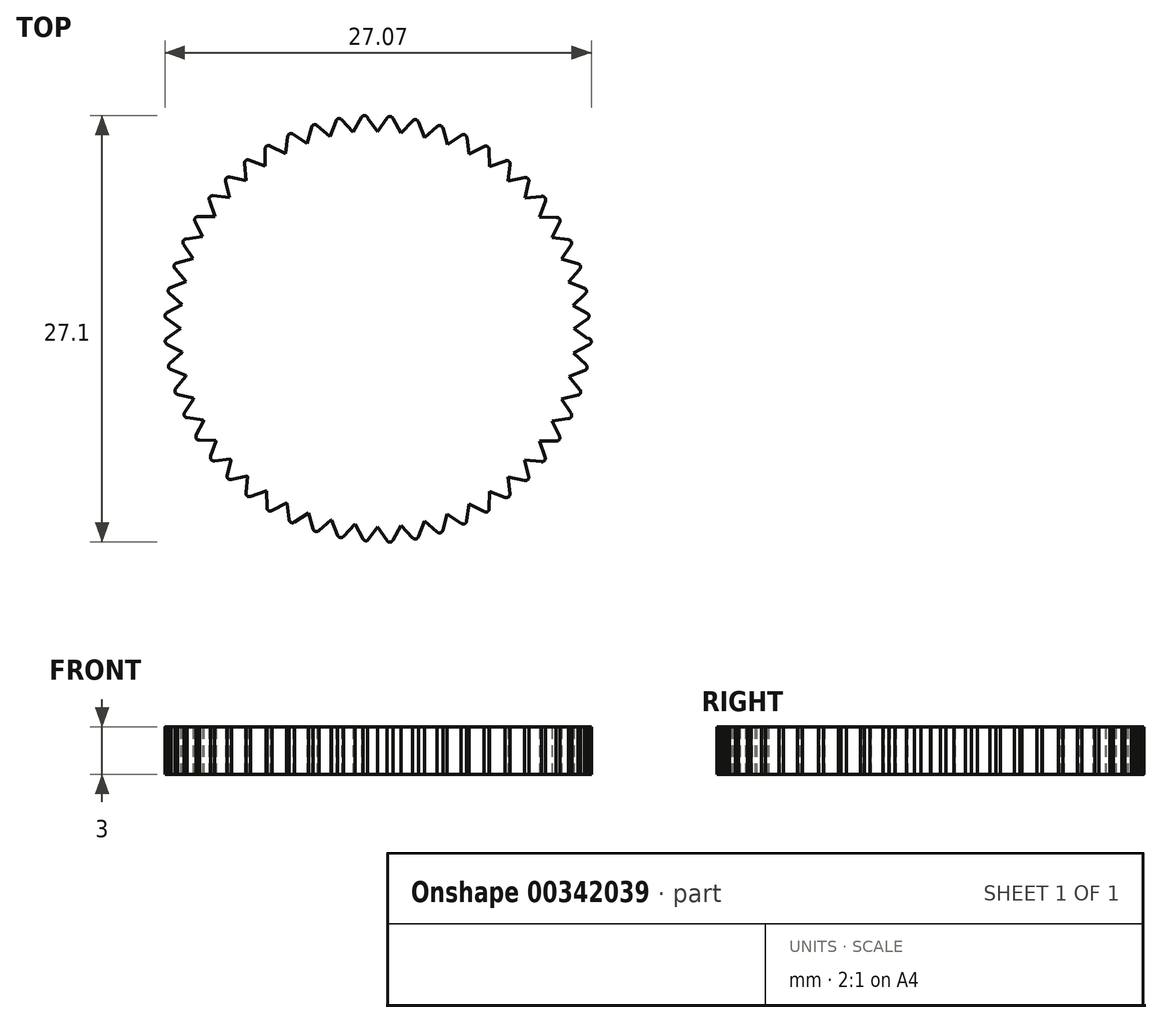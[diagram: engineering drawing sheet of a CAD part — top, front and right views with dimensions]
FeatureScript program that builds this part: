
annotation { "Feature Type Name" : "Feature", "Feature Type Description" : "" }
export const myFeature = defineFeature(function(context is Context, id is Id, definition is map)
    precondition{}
    {
        {
            var Q0;
            Q0=qCreatedBy(makeId("Top.planeOp"),FACE);
            var sketch = newSketch(context, id + "F0", { "sketchPlane" : qUnion([Q0])});
            skCircle(sketch, "E0", {"center": v(0, 0) * mm, "radius": 12.5 * mm});
            skPoint(sketch, "E1", {"position": v(1.51, 12.4) * mm});
            skPoint(sketch, "E2", {"position": v(0, 12.5) * mm});
            skArc(sketch, "E3", {"start": v(1, 13.35) * mm, "mid": v(0.82, 13.47) * mm, "end": v(0.62, 13.37) * mm});
            skLineSegment(sketch, "E4", {"start": v(0.62, 13.37) * mm, "end": v(0, 12.5) * mm});
            skLineSegment(sketch, "E5", {"start": v(1, 13.35) * mm, "end": v(1.51, 12.4) * mm});
            skPoint(sketch, "E6", {"position": v(3, 12.12) * mm});
            skArc(sketch, "E7", {"start": v(2.61, 13.12) * mm, "mid": v(2.45, 13.27) * mm, "end": v(2.24, 13.2) * mm});
            skLineSegment(sketch, "E8", {"start": v(2.24, 13.2) * mm, "end": v(1.51, 12.4) * mm});
            skLineSegment(sketch, "E9", {"start": v(2.61, 13.12) * mm, "end": v(3, 12.12) * mm});
            skPoint(sketch, "E10", {"position": v(4.45, 11.7) * mm});
            skArc(sketch, "E11", {"start": v(4.16, 12.72) * mm, "mid": v(4.01, 12.89) * mm, "end": v(3.8, 12.83) * mm});
            skLineSegment(sketch, "E12", {"start": v(3.8, 12.83) * mm, "end": v(3, 12.12) * mm});
            skLineSegment(sketch, "E13", {"start": v(4.16, 12.72) * mm, "end": v(4.45, 11.7) * mm});
            skPoint(sketch, "E14", {"position": v(5.82, 11.07) * mm});
            skArc(sketch, "E15", {"start": v(5.68, 12.13) * mm, "mid": v(5.56, 12.31) * mm, "end": v(5.34, 12.28) * mm});
            skLineSegment(sketch, "E16", {"start": v(5.34, 12.28) * mm, "end": v(4.45, 11.7) * mm});
            skLineSegment(sketch, "E17", {"start": v(5.68, 12.13) * mm, "end": v(5.82, 11.07) * mm});
            skPoint(sketch, "E18", {"position": v(7.12, 10.3) * mm});
            skArc(sketch, "E19", {"start": v(7.1, 11.36) * mm, "mid": v(7, 11.56) * mm, "end": v(6.78, 11.55) * mm});
            skLineSegment(sketch, "E20", {"start": v(6.78, 11.55) * mm, "end": v(5.82, 11.07) * mm});
            skLineSegment(sketch, "E21", {"start": v(7.1, 11.36) * mm, "end": v(7.12, 10.3) * mm});
            skPoint(sketch, "E22", {"position": v(8.3, 9.35) * mm});
            skArc(sketch, "E23", {"start": v(8.43, 10.41) * mm, "mid": v(8.35, 10.62) * mm, "end": v(8.13, 10.65) * mm});
            skLineSegment(sketch, "E24", {"start": v(8.13, 10.65) * mm, "end": v(7.12, 10.3) * mm});
            skLineSegment(sketch, "E25", {"start": v(8.43, 10.41) * mm, "end": v(8.3, 9.35) * mm});
            skPoint(sketch, "E26", {"position": v(9.37, 8.27) * mm});
            skArc(sketch, "E27", {"start": v(9.62, 9.3) * mm, "mid": v(9.57, 9.53) * mm, "end": v(9.35, 9.58) * mm});
            skLineSegment(sketch, "E28", {"start": v(9.35, 9.58) * mm, "end": v(8.3, 9.35) * mm});
            skLineSegment(sketch, "E29", {"start": v(9.62, 9.3) * mm, "end": v(9.37, 8.27) * mm});
            skPoint(sketch, "E30", {"position": v(10.32, 7.1) * mm});
            skArc(sketch, "E31", {"start": v(10.67, 8.1) * mm, "mid": v(10.64, 8.32) * mm, "end": v(10.43, 8.4) * mm});
            skLineSegment(sketch, "E32", {"start": v(10.43, 8.4) * mm, "end": v(9.37, 8.27) * mm});
            skLineSegment(sketch, "E33", {"start": v(10.67, 8.1) * mm, "end": v(10.32, 7.1) * mm});
            skPoint(sketch, "E34", {"position": v(11.08, 5.79) * mm});
            skArc(sketch, "E35", {"start": v(11.58, 6.74) * mm, "mid": v(11.58, 6.96) * mm, "end": v(11.38, 7.06) * mm});
            skLineSegment(sketch, "E36", {"start": v(11.38, 7.06) * mm, "end": v(10.32, 7.1) * mm});
            skLineSegment(sketch, "E37", {"start": v(11.58, 6.74) * mm, "end": v(11.08, 5.79) * mm});
            skPoint(sketch, "E38", {"position": v(11.7, 4.4) * mm});
            skArc(sketch, "E39", {"start": v(12.3, 5.3) * mm, "mid": v(12.33, 5.51) * mm, "end": v(12.14, 5.64) * mm});
            skLineSegment(sketch, "E40", {"start": v(12.14, 5.64) * mm, "end": v(11.08, 5.79) * mm});
            skLineSegment(sketch, "E41", {"start": v(12.3, 5.3) * mm, "end": v(11.7, 4.4) * mm});
            skPoint(sketch, "E42", {"position": v(12.13, 2.96) * mm});
            skArc(sketch, "E43", {"start": v(12.84, 3.76) * mm, "mid": v(12.9, 3.97) * mm, "end": v(12.73, 4.12) * mm});
            skLineSegment(sketch, "E44", {"start": v(12.73, 4.12) * mm, "end": v(11.7, 4.4) * mm});
            skLineSegment(sketch, "E45", {"start": v(12.84, 3.76) * mm, "end": v(12.13, 2.96) * mm});
            skPoint(sketch, "E46", {"position": v(12.42, 1.47) * mm});
            skArc(sketch, "E47", {"start": v(13.2, 2.2) * mm, "mid": v(13.28, 2.4) * mm, "end": v(13.13, 2.57) * mm});
            skLineSegment(sketch, "E48", {"start": v(13.13, 2.57) * mm, "end": v(12.13, 2.96) * mm});
            skLineSegment(sketch, "E49", {"start": v(13.2, 2.2) * mm, "end": v(12.42, 1.47) * mm});
            skPoint(sketch, "E50", {"position": v(12.48, 0) * mm});
            skArc(sketch, "E51", {"start": v(13.36, 0.61) * mm, "mid": v(13.44, 0.78) * mm, "end": v(13.36, 0.95) * mm});
            skLineSegment(sketch, "E52", {"start": v(13.36, 0.95) * mm, "end": v(12.42, 1.47) * mm});
            skLineSegment(sketch, "E53", {"start": v(13.36, 0.61) * mm, "end": v(12.48, 0) * mm});
            skPoint(sketch, "E54", {"position": v(12.46, -1.56) * mm});
            skArc(sketch, "E55", {"start": v(13.4, -1.05) * mm, "mid": v(13.59, -0.81) * mm, "end": v(13.35, -0.62) * mm});
            skLineSegment(sketch, "E56", {"start": v(13.35, -0.62) * mm, "end": v(12.48, 0) * mm});
            skLineSegment(sketch, "E57", {"start": v(13.4, -1.05) * mm, "end": v(12.46, -1.56) * mm});
            skPoint(sketch, "E58", {"position": v(12.17, -3.05) * mm});
            skArc(sketch, "E59", {"start": v(13.17, -2.67) * mm, "mid": v(13.32, -2.5) * mm, "end": v(13.24, -2.3) * mm});
            skLineSegment(sketch, "E60", {"start": v(13.24, -2.3) * mm, "end": v(12.46, -1.56) * mm});
            skLineSegment(sketch, "E61", {"start": v(13.17, -2.67) * mm, "end": v(12.17, -3.05) * mm});
            skPoint(sketch, "E62", {"position": v(11.7, -4.49) * mm});
            skArc(sketch, "E63", {"start": v(12.74, -4.23) * mm, "mid": v(12.9, -4.09) * mm, "end": v(12.86, -3.87) * mm});
            skLineSegment(sketch, "E64", {"start": v(12.86, -3.87) * mm, "end": v(12.17, -3.05) * mm});
            skLineSegment(sketch, "E65", {"start": v(12.74, -4.23) * mm, "end": v(11.7, -4.49) * mm});
            skPoint(sketch, "E66", {"position": v(11.1, -5.87) * mm});
            skArc(sketch, "E67", {"start": v(12.15, -5.72) * mm, "mid": v(12.33, -5.6) * mm, "end": v(12.3, -5.37) * mm});
            skLineSegment(sketch, "E68", {"start": v(12.3, -5.37) * mm, "end": v(11.7, -4.49) * mm});
            skLineSegment(sketch, "E69", {"start": v(12.15, -5.72) * mm, "end": v(11.1, -5.87) * mm});
            skPoint(sketch, "E70", {"position": v(10.3, -7.16) * mm});
            skArc(sketch, "E71", {"start": v(11.36, -7.16) * mm, "mid": v(11.56, -7.06) * mm, "end": v(11.56, -6.83) * mm});
            skLineSegment(sketch, "E72", {"start": v(11.56, -6.83) * mm, "end": v(11.1, -5.87) * mm});
            skLineSegment(sketch, "E73", {"start": v(11.36, -7.16) * mm, "end": v(10.3, -7.16) * mm});
            skPoint(sketch, "E74", {"position": v(-11.02, -5.81) * mm});
            skPoint(sketch, "E75", {"position": v(-10.23, -7.1) * mm});
            skArc(sketch, "E76", {"start": v(-11.5, -6.77) * mm, "mid": v(-11.5, -7) * mm, "end": v(-11.3, -7.1) * mm});
            skLineSegment(sketch, "E77", {"start": v(-11.3, -7.1) * mm, "end": v(-10.23, -7.1) * mm});
            skLineSegment(sketch, "E78", {"start": v(-11.5, -6.77) * mm, "end": v(-11.02, -5.81) * mm});
            skPoint(sketch, "E79", {"position": v(-11.64, -4.43) * mm});
            skArc(sketch, "E80", {"start": v(-12.23, -5.32) * mm, "mid": v(-12.26, -5.54) * mm, "end": v(-12.08, -5.66) * mm});
            skLineSegment(sketch, "E81", {"start": v(-12.08, -5.66) * mm, "end": v(-11.02, -5.81) * mm});
            skLineSegment(sketch, "E82", {"start": v(-12.23, -5.32) * mm, "end": v(-11.64, -4.43) * mm});
            skPoint(sketch, "E83", {"position": v(-12.12, -3) * mm});
            skArc(sketch, "E84", {"start": v(-12.8, -3.82) * mm, "mid": v(-12.85, -4.04) * mm, "end": v(-12.68, -4.18) * mm});
            skLineSegment(sketch, "E85", {"start": v(-12.68, -4.18) * mm, "end": v(-11.64, -4.43) * mm});
            skLineSegment(sketch, "E86", {"start": v(-12.8, -3.82) * mm, "end": v(-12.12, -3) * mm});
            skPoint(sketch, "E87", {"position": v(-12.4, -1.5) * mm});
            skArc(sketch, "E88", {"start": v(-13.18, -2.23) * mm, "mid": v(-13.26, -2.44) * mm, "end": v(-13.11, -2.6) * mm});
            skLineSegment(sketch, "E89", {"start": v(-13.11, -2.6) * mm, "end": v(-12.12, -3) * mm});
            skLineSegment(sketch, "E90", {"start": v(-13.18, -2.23) * mm, "end": v(-12.4, -1.5) * mm});
            skPoint(sketch, "E91", {"position": v(-12.5, 0) * mm});
            skArc(sketch, "E92", {"start": v(-13.37, -0.63) * mm, "mid": v(-13.47, -0.83) * mm, "end": v(-13.34, -1) * mm});
            skLineSegment(sketch, "E93", {"start": v(-13.34, -1) * mm, "end": v(-12.4, -1.5) * mm});
            skLineSegment(sketch, "E94", {"start": v(-13.37, -0.63) * mm, "end": v(-12.5, 0) * mm});
            skPoint(sketch, "E95", {"position": v(-12.41, 1.51) * mm});
            skArc(sketch, "E96", {"start": v(-13.35, 1) * mm, "mid": v(-13.48, 0.82) * mm, "end": v(-13.38, 0.62) * mm});
            skLineSegment(sketch, "E97", {"start": v(-13.38, 0.62) * mm, "end": v(-12.5, 0) * mm});
            skLineSegment(sketch, "E98", {"start": v(-13.35, 1) * mm, "end": v(-12.41, 1.51) * mm});
            skPoint(sketch, "E99", {"position": v(-12.14, 3) * mm});
            skArc(sketch, "E100", {"start": v(-13.13, 2.6) * mm, "mid": v(-13.28, 2.44) * mm, "end": v(-13.2, 2.23) * mm});
            skLineSegment(sketch, "E101", {"start": v(-13.2, 2.23) * mm, "end": v(-12.41, 1.51) * mm});
            skLineSegment(sketch, "E102", {"start": v(-13.13, 2.6) * mm, "end": v(-12.14, 3) * mm});
            skPoint(sketch, "E103", {"position": v(-11.71, 4.45) * mm});
            skArc(sketch, "E104", {"start": v(-12.74, 4.16) * mm, "mid": v(-12.9, 4.01) * mm, "end": v(-12.85, 3.8) * mm});
            skLineSegment(sketch, "E105", {"start": v(-12.85, 3.8) * mm, "end": v(-12.14, 3) * mm});
            skLineSegment(sketch, "E106", {"start": v(-12.74, 4.16) * mm, "end": v(-11.71, 4.45) * mm});
            skPoint(sketch, "E107", {"position": v(-11.09, 5.83) * mm});
            skArc(sketch, "E108", {"start": v(-12.15, 5.69) * mm, "mid": v(-12.33, 5.56) * mm, "end": v(-12.3, 5.34) * mm});
            skLineSegment(sketch, "E109", {"start": v(-12.3, 5.34) * mm, "end": v(-11.71, 4.45) * mm});
            skLineSegment(sketch, "E110", {"start": v(-12.15, 5.69) * mm, "end": v(-11.09, 5.83) * mm});
            skPoint(sketch, "E111", {"position": v(-10.3, 7.13) * mm});
            skArc(sketch, "E112", {"start": v(-11.38, 7.1) * mm, "mid": v(-11.57, 7) * mm, "end": v(-11.57, 6.78) * mm});
            skLineSegment(sketch, "E113", {"start": v(-11.57, 6.78) * mm, "end": v(-11.09, 5.83) * mm});
            skLineSegment(sketch, "E114", {"start": v(-11.38, 7.1) * mm, "end": v(-10.3, 7.13) * mm});
            skPoint(sketch, "E115", {"position": v(-9.37, 8.31) * mm});
            skArc(sketch, "E116", {"start": v(-10.43, 8.43) * mm, "mid": v(-10.64, 8.35) * mm, "end": v(-10.67, 8.13) * mm});
            skLineSegment(sketch, "E117", {"start": v(-10.67, 8.13) * mm, "end": v(-10.3, 7.13) * mm});
            skLineSegment(sketch, "E118", {"start": v(-10.43, 8.43) * mm, "end": v(-9.37, 8.31) * mm});
            skPoint(sketch, "E119", {"position": v(-8.32, 9.4) * mm});
            skArc(sketch, "E120", {"start": v(-9.36, 9.62) * mm, "mid": v(-9.58, 9.57) * mm, "end": v(-9.63, 9.35) * mm});
            skLineSegment(sketch, "E121", {"start": v(-9.63, 9.35) * mm, "end": v(-9.37, 8.31) * mm});
            skLineSegment(sketch, "E122", {"start": v(-9.36, 9.62) * mm, "end": v(-8.32, 9.4) * mm});
            skPoint(sketch, "E123", {"position": v(-7.13, 10.33) * mm});
            skArc(sketch, "E124", {"start": v(-8.13, 10.7) * mm, "mid": v(-8.35, 10.67) * mm, "end": v(-8.43, 10.46) * mm});
            skLineSegment(sketch, "E125", {"start": v(-8.43, 10.46) * mm, "end": v(-8.32, 9.4) * mm});
            skLineSegment(sketch, "E126", {"start": v(-8.13, 10.7) * mm, "end": v(-7.13, 10.33) * mm});
            skPoint(sketch, "E127", {"position": v(-5.84, 11.13) * mm});
            skArc(sketch, "E128", {"start": v(-6.8, 11.6) * mm, "mid": v(-7.02, 11.6) * mm, "end": v(-7.12, 11.4) * mm});
            skLineSegment(sketch, "E129", {"start": v(-7.12, 11.4) * mm, "end": v(-7.13, 10.33) * mm});
            skLineSegment(sketch, "E130", {"start": v(-6.8, 11.6) * mm, "end": v(-5.84, 11.13) * mm});
            skPoint(sketch, "E131", {"position": v(-4.46, 11.74) * mm});
            skArc(sketch, "E132", {"start": v(-5.34, 12.34) * mm, "mid": v(-5.56, 12.37) * mm, "end": v(-5.69, 12.19) * mm});
            skLineSegment(sketch, "E133", {"start": v(-5.69, 12.19) * mm, "end": v(-5.84, 11.13) * mm});
            skLineSegment(sketch, "E134", {"start": v(-5.34, 12.34) * mm, "end": v(-4.46, 11.74) * mm});
            skPoint(sketch, "E135", {"position": v(-3.01, 12.18) * mm});
            skArc(sketch, "E136", {"start": v(-3.82, 12.89) * mm, "mid": v(-4.03, 12.94) * mm, "end": v(-4.18, 12.78) * mm});
            skLineSegment(sketch, "E137", {"start": v(-4.18, 12.78) * mm, "end": v(-4.46, 11.74) * mm});
            skLineSegment(sketch, "E138", {"start": v(-3.82, 12.89) * mm, "end": v(-3.01, 12.18) * mm});
            skPoint(sketch, "E139", {"position": v(-1.53, 12.48) * mm});
            skArc(sketch, "E140", {"start": v(-2.26, 13.26) * mm, "mid": v(-2.47, 13.33) * mm, "end": v(-2.63, 13.18) * mm});
            skLineSegment(sketch, "E141", {"start": v(-2.63, 13.18) * mm, "end": v(-3.01, 12.18) * mm});
            skLineSegment(sketch, "E142", {"start": v(-2.26, 13.26) * mm, "end": v(-1.53, 12.48) * mm});
            skArc(sketch, "E143", {"start": v(-0.61, 13.38) * mm, "mid": v(-0.8, 13.53) * mm, "end": v(-1, 13.41) * mm});
            skLineSegment(sketch, "E144", {"start": v(-1, 13.41) * mm, "end": v(-1.53, 12.48) * mm});
            skLineSegment(sketch, "E145", {"start": v(-0.61, 13.38) * mm, "end": v(0, 12.5) * mm});
            skPoint(sketch, "E146", {"position": v(-1.42, -12.42) * mm});
            skPoint(sketch, "E147", {"position": v(0, -12.6) * mm});
            skArc(sketch, "E148", {"start": v(-0.91, -13.36) * mm, "mid": v(-0.79, -13.47) * mm, "end": v(-0.62, -13.46) * mm});
            skLineSegment(sketch, "E149", {"start": v(-0.62, -13.46) * mm, "end": v(0, -12.6) * mm});
            skLineSegment(sketch, "E150", {"start": v(-0.91, -13.36) * mm, "end": v(-1.42, -12.42) * mm});
            skPoint(sketch, "E151", {"position": v(-2.9, -12.13) * mm});
            skArc(sketch, "E152", {"start": v(-2.52, -13.13) * mm, "mid": v(-2.36, -13.28) * mm, "end": v(-2.15, -13.2) * mm});
            skLineSegment(sketch, "E153", {"start": v(-2.15, -13.2) * mm, "end": v(-1.42, -12.42) * mm});
            skLineSegment(sketch, "E154", {"start": v(-2.52, -13.13) * mm, "end": v(-2.9, -12.13) * mm});
            skPoint(sketch, "E155", {"position": v(-4.36, -11.7) * mm});
            skArc(sketch, "E156", {"start": v(-4.07, -12.73) * mm, "mid": v(-3.92, -12.9) * mm, "end": v(-3.7, -12.84) * mm});
            skLineSegment(sketch, "E157", {"start": v(-3.7, -12.84) * mm, "end": v(-2.9, -12.13) * mm});
            skLineSegment(sketch, "E158", {"start": v(-4.07, -12.73) * mm, "end": v(-4.36, -11.7) * mm});
            skPoint(sketch, "E159", {"position": v(-5.74, -11.08) * mm});
            skArc(sketch, "E160", {"start": v(-5.6, -12.14) * mm, "mid": v(-5.47, -12.32) * mm, "end": v(-5.25, -12.3) * mm});
            skLineSegment(sketch, "E161", {"start": v(-5.25, -12.3) * mm, "end": v(-4.36, -11.7) * mm});
            skLineSegment(sketch, "E162", {"start": v(-5.6, -12.14) * mm, "end": v(-5.74, -11.08) * mm});
            skPoint(sketch, "E163", {"position": v(-7.04, -10.3) * mm});
            skArc(sketch, "E164", {"start": v(-7.01, -11.37) * mm, "mid": v(-6.9, -11.57) * mm, "end": v(-6.69, -11.56) * mm});
            skLineSegment(sketch, "E165", {"start": v(-6.69, -11.56) * mm, "end": v(-5.74, -11.08) * mm});
            skLineSegment(sketch, "E166", {"start": v(-7.01, -11.37) * mm, "end": v(-7.04, -10.3) * mm});
            skPoint(sketch, "E167", {"position": v(-8.22, -9.36) * mm});
            skArc(sketch, "E168", {"start": v(-8.34, -10.42) * mm, "mid": v(-8.26, -10.63) * mm, "end": v(-8.04, -10.66) * mm});
            skLineSegment(sketch, "E169", {"start": v(-8.04, -10.66) * mm, "end": v(-7.04, -10.3) * mm});
            skLineSegment(sketch, "E170", {"start": v(-8.34, -10.42) * mm, "end": v(-8.22, -9.36) * mm});
            skPoint(sketch, "E171", {"position": v(-9.28, -8.28) * mm});
            skArc(sketch, "E172", {"start": v(-9.53, -9.32) * mm, "mid": v(-9.48, -9.54) * mm, "end": v(-9.26, -9.59) * mm});
            skLineSegment(sketch, "E173", {"start": v(-9.26, -9.59) * mm, "end": v(-8.22, -9.36) * mm});
            skLineSegment(sketch, "E174", {"start": v(-9.53, -9.32) * mm, "end": v(-9.28, -8.28) * mm});
            skArc(sketch, "E175", {"start": v(-10.58, -8.11) * mm, "mid": v(-10.55, -8.33) * mm, "end": v(-10.34, -8.4) * mm});
            skLineSegment(sketch, "E176", {"start": v(-10.34, -8.4) * mm, "end": v(-9.28, -8.28) * mm});
            skLineSegment(sketch, "E177", {"start": v(-10.58, -8.11) * mm, "end": v(-10.23, -7.1) * mm});
            skPoint(sketch, "E178", {"position": v(9.35, -8.34) * mm});
            skArc(sketch, "E179", {"start": v(10.42, -8.46) * mm, "mid": v(10.62, -8.38) * mm, "end": v(10.65, -8.16) * mm});
            skLineSegment(sketch, "E180", {"start": v(10.65, -8.16) * mm, "end": v(10.3, -7.16) * mm});
            skLineSegment(sketch, "E181", {"start": v(10.42, -8.46) * mm, "end": v(9.35, -8.34) * mm});
            skPoint(sketch, "E182", {"position": v(8.3, -9.43) * mm});
            skArc(sketch, "E183", {"start": v(9.35, -9.65) * mm, "mid": v(9.56, -9.6) * mm, "end": v(9.61, -9.38) * mm});
            skLineSegment(sketch, "E184", {"start": v(9.61, -9.38) * mm, "end": v(9.35, -8.34) * mm});
            skLineSegment(sketch, "E185", {"start": v(9.35, -9.65) * mm, "end": v(8.3, -9.43) * mm});
            skPoint(sketch, "E186", {"position": v(7.11, -10.36) * mm});
            skArc(sketch, "E187", {"start": v(8.12, -10.73) * mm, "mid": v(8.34, -10.7) * mm, "end": v(8.41, -10.5) * mm});
            skLineSegment(sketch, "E188", {"start": v(8.41, -10.5) * mm, "end": v(8.3, -9.43) * mm});
            skLineSegment(sketch, "E189", {"start": v(8.12, -10.73) * mm, "end": v(7.11, -10.36) * mm});
            skPoint(sketch, "E190", {"position": v(5.82, -11.16) * mm});
            skArc(sketch, "E191", {"start": v(6.78, -11.63) * mm, "mid": v(7, -11.63) * mm, "end": v(7.1, -11.43) * mm});
            skLineSegment(sketch, "E192", {"start": v(7.1, -11.43) * mm, "end": v(7.11, -10.36) * mm});
            skLineSegment(sketch, "E193", {"start": v(6.78, -11.63) * mm, "end": v(5.82, -11.16) * mm});
            skPoint(sketch, "E194", {"position": v(4.44, -11.77) * mm});
            skArc(sketch, "E195", {"start": v(5.33, -12.37) * mm, "mid": v(5.55, -12.4) * mm, "end": v(5.67, -12.22) * mm});
            skLineSegment(sketch, "E196", {"start": v(5.67, -12.22) * mm, "end": v(5.82, -11.16) * mm});
            skLineSegment(sketch, "E197", {"start": v(5.33, -12.37) * mm, "end": v(4.44, -11.77) * mm});
            skPoint(sketch, "E198", {"position": v(3, -12.22) * mm});
            skArc(sketch, "E199", {"start": v(3.8, -12.92) * mm, "mid": v(4.02, -12.97) * mm, "end": v(4.16, -12.8) * mm});
            skLineSegment(sketch, "E200", {"start": v(4.16, -12.8) * mm, "end": v(4.44, -11.77) * mm});
            skLineSegment(sketch, "E201", {"start": v(3.8, -12.92) * mm, "end": v(3, -12.22) * mm});
            skPoint(sketch, "E202", {"position": v(1.51, -12.51) * mm});
            skArc(sketch, "E203", {"start": v(2.24, -13.29) * mm, "mid": v(2.45, -13.37) * mm, "end": v(2.61, -13.21) * mm});
            skLineSegment(sketch, "E204", {"start": v(2.61, -13.21) * mm, "end": v(3, -12.22) * mm});
            skLineSegment(sketch, "E205", {"start": v(2.24, -13.29) * mm, "end": v(1.51, -12.51) * mm});
            skArc(sketch, "E206", {"start": v(0.61, -13.47) * mm, "mid": v(0.8, -13.57) * mm, "end": v(1, -13.45) * mm});
            skLineSegment(sketch, "E207", {"start": v(1, -13.45) * mm, "end": v(1.51, -12.51) * mm});
            skLineSegment(sketch, "E208", {"start": v(0.61, -13.47) * mm, "end": v(0, -12.6) * mm});
            skSolve(sketch);
        }
        {
            var Q0;
            Q0 = qSketchRegion(id + "F0", true);
            extrude(context, id + "F1", {"entities" : qUnion([Q0]), "depth" : 3 * mm});
        }
    });
